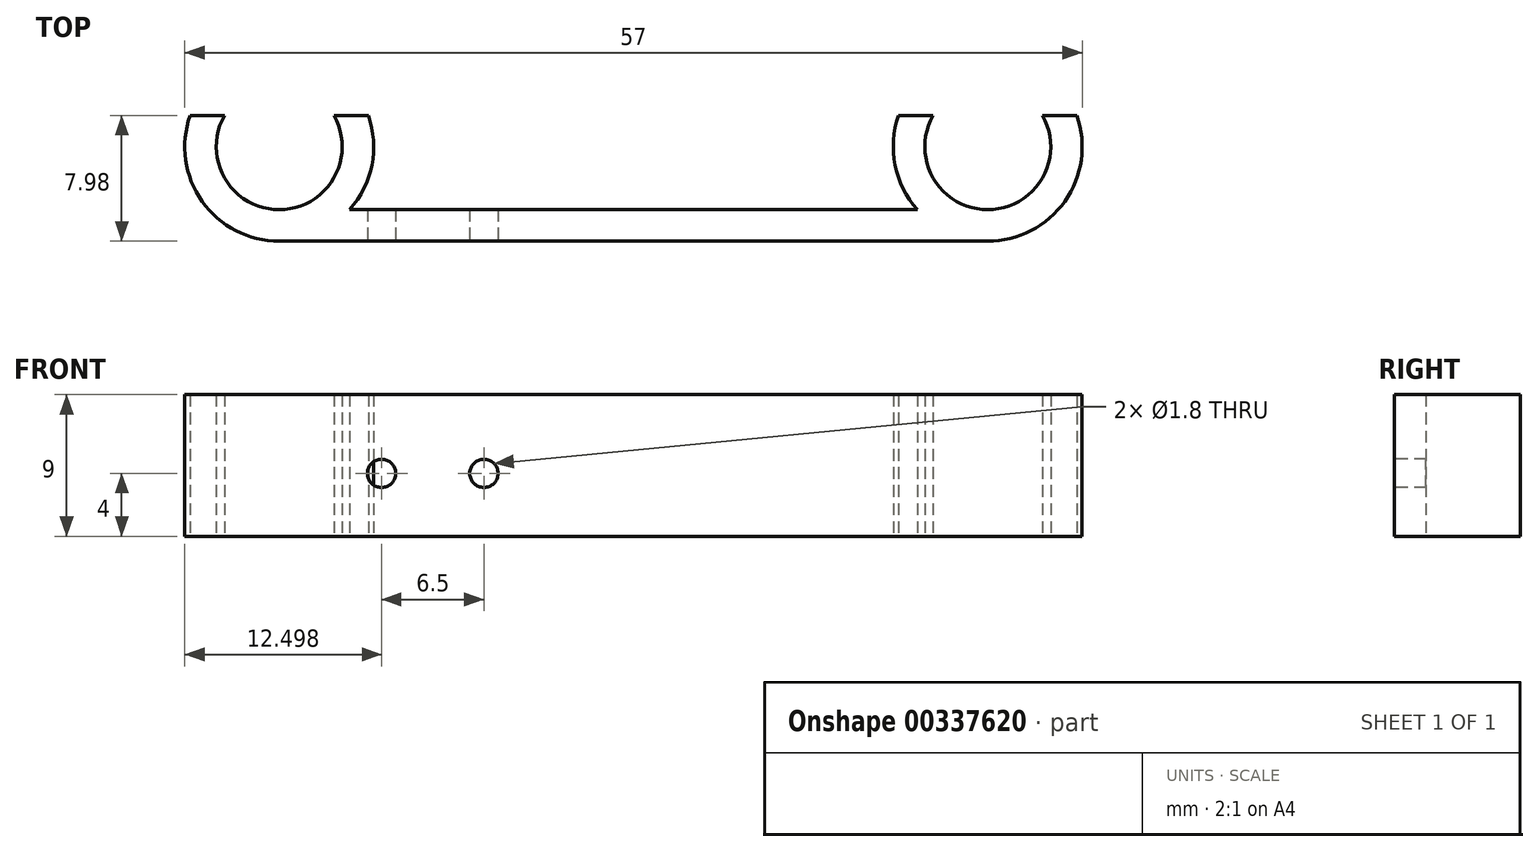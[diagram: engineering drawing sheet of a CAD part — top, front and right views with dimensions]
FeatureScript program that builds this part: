
annotation { "Feature Type Name" : "Feature", "Feature Type Description" : "" }
export const myFeature = defineFeature(function(context is Context, id is Id, definition is map)
    precondition{}
    {
        {
            var Q0;
            Q0=qCreatedBy(makeId("Top.planeOp"),FACE);
            var sketch = newSketch(context, id + "F0", { "sketchPlane" : qUnion([Q0])});
            skArc(sketch, "E0", {"start": v(-19.73, 7.98) * mm, "mid": v(-14.06, 0) * mm, "end": v(-8.4, 7.98) * mm});
            skLineSegment(sketch, "E1.right", {"start": v(278.54, 89.36) * mm, "end": v(278.54, 0) * mm});
            skArc(sketch, "E2", {"start": v(-17.54, 7.98) * mm, "mid": v(-14.06, 2) * mm, "end": v(-10.59, 7.98) * mm});
            skLineSegment(sketch, "E3.top", {"start": v(-19.73, 7.98) * mm, "end": v(-17.54, 7.98) * mm});
            skLineSegment(sketch, "E4.trimOffspring", {"start": v(-10.59, 7.98) * mm, "end": v(-8.4, 7.98) * mm});
            skArc(sketch, "E5", {"start": v(25.27, 7.98) * mm, "mid": v(30.94, 0) * mm, "end": v(36.6, 7.98) * mm});
            skArc(sketch, "E6", {"start": v(27.46, 7.98) * mm, "mid": v(30.94, 2) * mm, "end": v(34.41, 7.98) * mm});
            skLineSegment(sketch, "E7.top", {"start": v(25.27, 7.98) * mm, "end": v(27.46, 7.98) * mm});
            skLineSegment(sketch, "E8.trimOffspring", {"start": v(34.41, 7.98) * mm, "end": v(36.6, 7.98) * mm});
            skLineSegment(sketch, "E9.bottom", {"start": v(-14.06, 0) * mm, "end": v(30.94, 0) * mm});
            skLineSegment(sketch, "E10", {"start": v(-14.06, 0) * mm, "end": v(-14.06, 2) * mm});
            skLineSegment(sketch, "E11", {"start": v(-14.06, 2) * mm, "end": v(30.94, 2) * mm});
            skLineSegment(sketch, "E12", {"start": v(30.94, 2) * mm, "end": v(30.94, 0) * mm});
            skSolve(sketch);
        }
        {
            var Q0;
            Q0 = qSketchRegion(id + "F0", true);
            extrude(context, id + "F1", {"entities" : qUnion([Q0]), "depth" : 9 * mm});
        }
        {
            var Q0;
            Q0=qCreatedBy(makeId("Front.planeOp"),FACE);
            var sketch = newSketch(context, id + "F2", { "sketchPlane" : qUnion([Q0])});
            skCircle(sketch, "E13", {"center": v(-7.56, 4) * mm, "radius": 0.9 * mm});
            skCircle(sketch, "E14", {"center": v(-1.06, 4) * mm, "radius": 0.9 * mm});
            skSolve(sketch);
        }
        {
            var Q0;
            Q0 = qSketchRegion(id + "F2", true);
            extrude(context, id + "F3", {"entities" : qUnion([Q0]), "operationType" : NewBodyOperationType.REMOVE, "oppositeDirection" : true, "depth" : 2 * mm});
        }
    });
